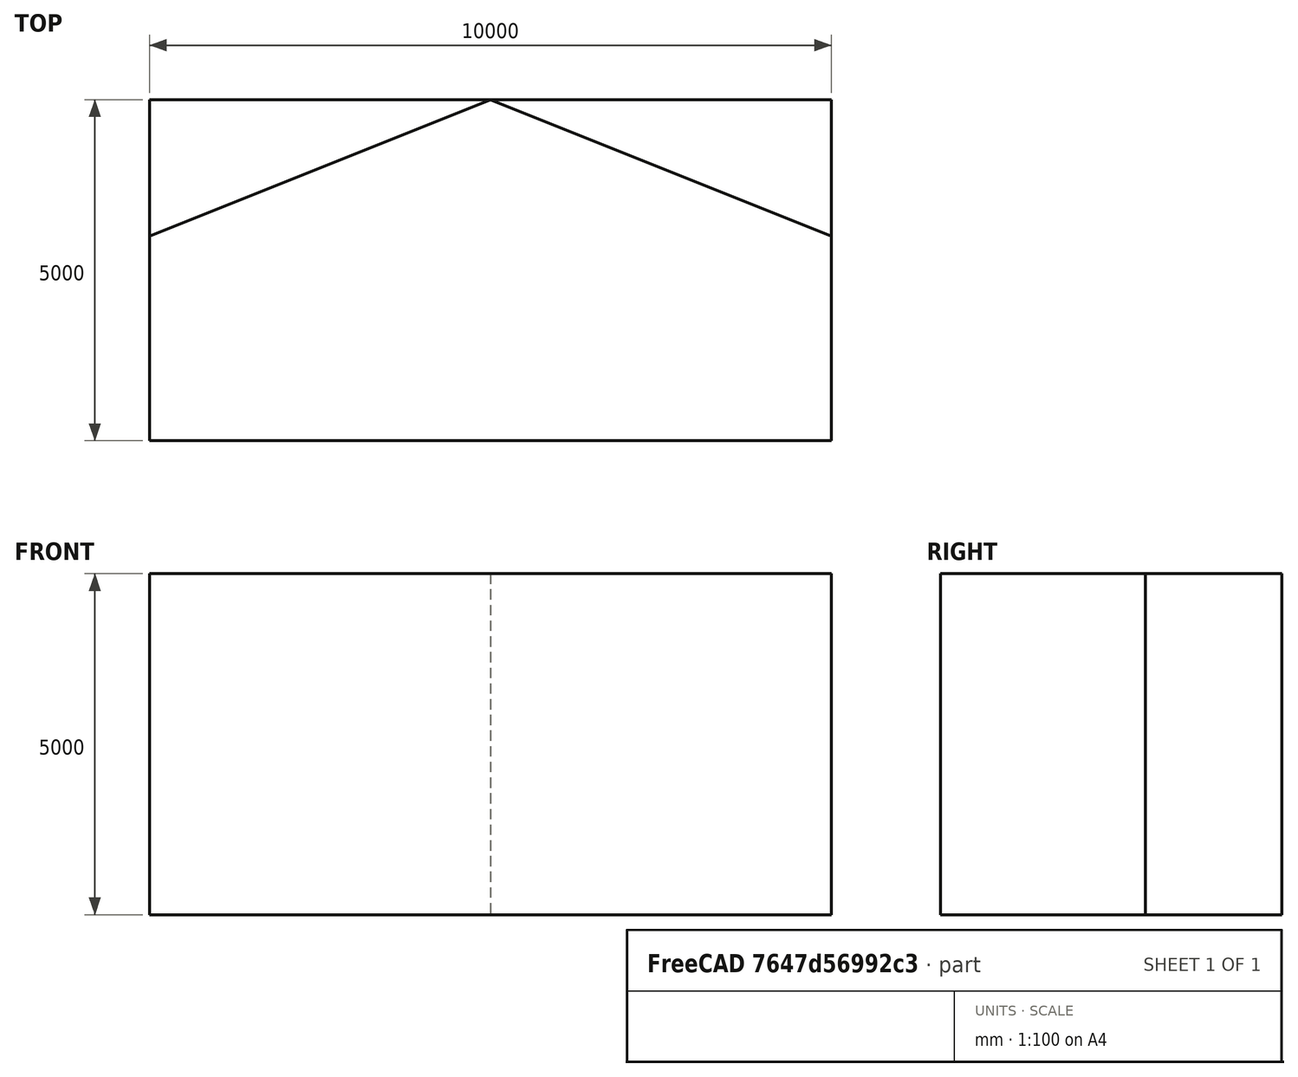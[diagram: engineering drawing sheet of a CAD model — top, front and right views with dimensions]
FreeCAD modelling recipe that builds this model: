
FCSTD DOCUMENT  (FreeCAD 0.18.3R)
Label: Edificio
License: All rights reserved
LicenseURL: http://en.wikipedia.org/wiki/All_rights_reserved
objects: Part::Plane×5, Part::Part2DObjectPython×5, Part::Feature×2
note: 12 computed .brp shape members not serialized (recipe doc carries the construction recipe); baked Part::Feature solids carry a one-line shape summary decoded from their .brp

FEATURE [Part::Plane] Plane
  AttacherType = Attacher::AttachEngine3D
  Length = 5000
  Placement = pos=(-5000,0,-2500) rot=(0.57735,0.57735,0.57735;4.18879rad)
  Width = 10000
FEATURE [Part::Plane] Plane005
  AttacherType = Attacher::AttachEngine3D
  Length = 3000
  Placement = pos=(-5000,0,-2500) rot=(0.57735,0.57735,0.57735;2.0944rad)
  Width = 5000
FEATURE [Part::Plane] Plane006
  AttacherType = Attacher::AttachEngine3D
  Length = 3000
  Placement = pos=(5000,0,-2500) rot=(0.57735,0.57735,0.57735;2.0944rad)
  Width = 5000
FEATURE [Part::Plane] Plane008
  AttacherType = Attacher::AttachEngine3D
  Length = 10000
  Placement = pos=(-5000,0,-2500) rot=(0,0,1;0rad)
  Width = 5000
FEATURE [Part::Plane] Plane010
  AttacherType = Attacher::AttachEngine3D
  Length = 10000
  Placement = pos=(-5000,0,2500) rot=(0,0,1;0rad)
  Width = 5000
FEATURE [Part::Part2DObjectPython] Line  # Draft 2D object (typed FeaturePython)
  ChamferSize = 0
  Closed = false
  End = (0,5000,-2500)
  FilletRadius = 0
  Length = 5000
  MakeFace = false
  Placement = pos=(0,5000,2500) rot=(0,0,1;0rad)
  Points = (2) [(0,0,0),(0,0,-5000)]
  Start = (0,5000,2500)
  Subdivisions = 0
FEATURE [Part::Part2DObjectPython] Line001  # Draft 2D object (typed FeaturePython)
  ChamferSize = 0
  Closed = false
  End = (5000,3000,-2500)
  FilletRadius = 0
  Length = 5385.16
  MakeFace = false
  Placement = pos=(0,5000,-2500) rot=(0,0,1;0rad)
  Points = (2) [(0,0,0),(5000,-2000,0)]
  Start = (0,5000,-2500)
  Subdivisions = 0
FEATURE [Part::Part2DObjectPython] Line002  # Draft 2D object (typed FeaturePython)
  ChamferSize = 0
  Closed = false
  End = (5000,3000,2500)
  FilletRadius = 0
  Length = 5385.16
  MakeFace = false
  Placement = pos=(0,5000,2500) rot=(0,0,1;0rad)
  Points = (2) [(0,0,0),(5000,-2000,0)]
  Start = (0,5000,2500)
  Subdivisions = 0
FEATURE [Part::Part2DObjectPython] Line003  # Draft 2D object (typed FeaturePython)
  ChamferSize = 0
  Closed = false
  End = (-5000,3000,-2500)
  FilletRadius = 0
  Length = 5385.16
  MakeFace = false
  Placement = pos=(0,5000,-2500) rot=(0,0,1;0rad)
  Points = (2) [(0,0,0),(-5000,-2000,0)]
  Start = (0,5000,-2500)
  Subdivisions = 0
FEATURE [Part::Part2DObjectPython] Line004  # Draft 2D object (typed FeaturePython)
  ChamferSize = 0
  Closed = false
  End = (-5000,3000,2500)
  FilletRadius = 0
  Length = 5385.16
  MakeFace = false
  Placement = pos=(0,5000,2500) rot=(0,0,1;0rad)
  Points = (2) [(0,0,0),(-5000,-2000,0)]
  Start = (0,5000,2500)
  Subdivisions = 0
FEATURE [Part::Feature] Face
  shape: bbox 5500 x 2200 x 5500 mm, 1 faces, 0 solids (baked)
FEATURE [Part::Feature] Face001
  shape: bbox 5500 x 2200 x 5500 mm, 1 faces, 0 solids (baked)
